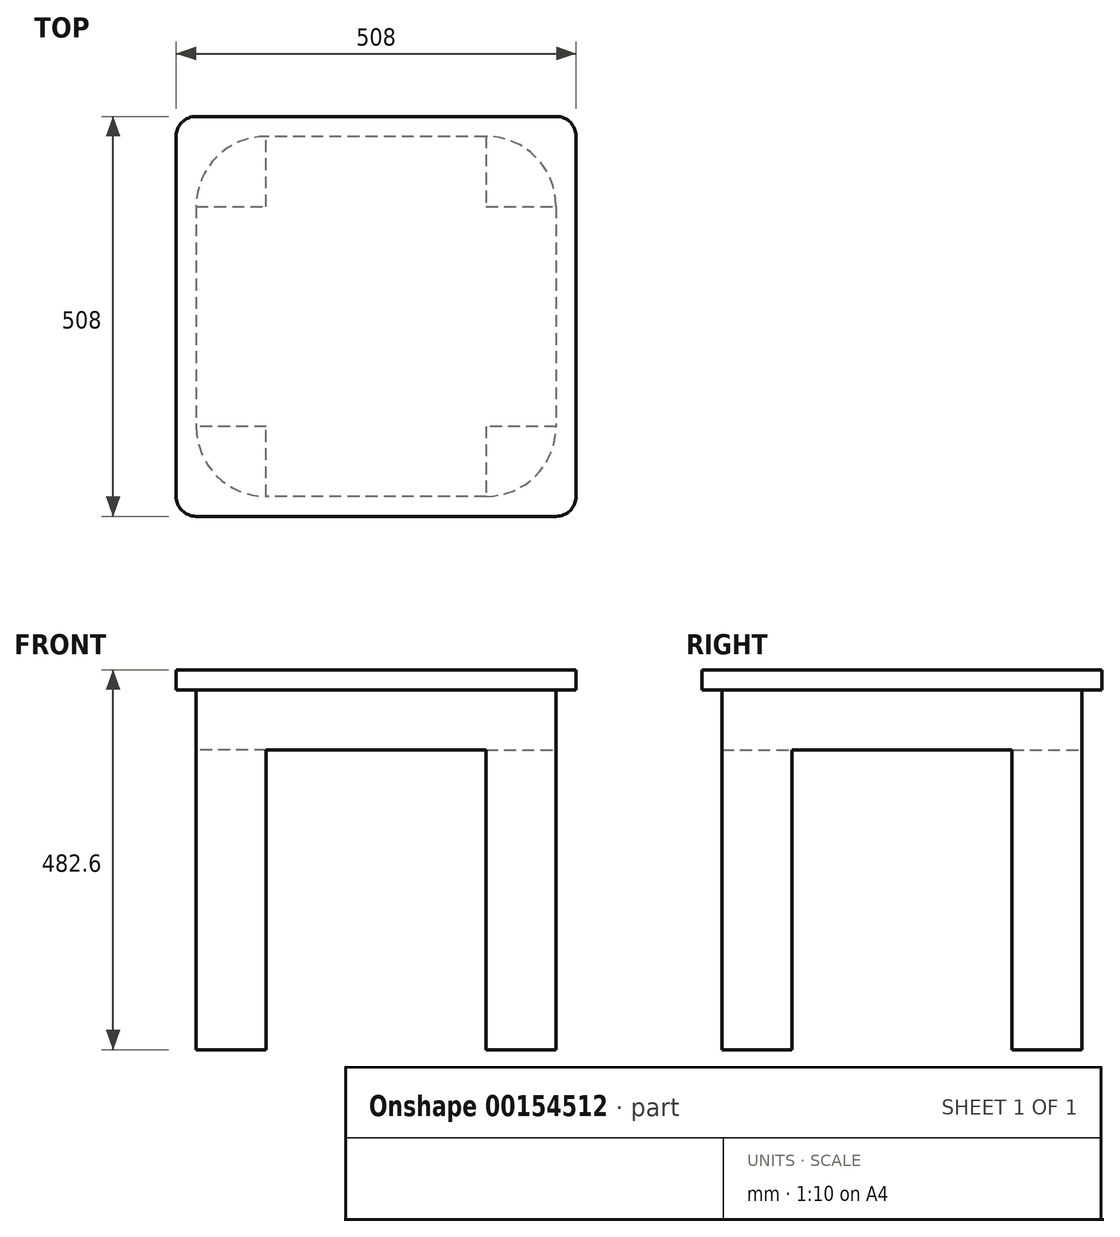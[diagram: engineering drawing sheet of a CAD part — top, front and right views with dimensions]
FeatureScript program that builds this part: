
annotation { "Feature Type Name" : "Feature", "Feature Type Description" : "" }
export const myFeature = defineFeature(function(context is Context, id is Id, definition is map)
    precondition{}
    {
        {
            var Q0;
            Q0=qCreatedBy(makeId("Top.planeOp"),FACE);
            var sketch = newSketch(context, id + "F0", { "sketchPlane" : qUnion([Q0])});
            skLineSegment(sketch, "E0.bottom", {"start": v(254, 254) * mm, "end": v(-254, 254) * mm});
            skLineSegment(sketch, "E0.top", {"start": v(254, -254) * mm, "end": v(-254, -254) * mm});
            skLineSegment(sketch, "E0.left", {"start": v(254, 254) * mm, "end": v(254, -254) * mm});
            skLineSegment(sketch, "E0.right", {"start": v(-254, 254) * mm, "end": v(-254, -254) * mm});
            skPoint(sketch, "E0.middle", {"position": v(0, 0) * mm});
            skLineSegment(sketch, "E1.bottom", {"start": v(228.6, 228.6) * mm, "end": v(-228.6, 228.6) * mm});
            skLineSegment(sketch, "E1.top", {"start": v(228.6, -228.6) * mm, "end": v(-228.6, -228.6) * mm});
            skLineSegment(sketch, "E1.left", {"start": v(228.6, 228.6) * mm, "end": v(228.6, -228.6) * mm});
            skLineSegment(sketch, "E1.right", {"start": v(-228.6, 228.6) * mm, "end": v(-228.6, -228.6) * mm});
            skLineSegment(sketch, "E2", {"start": v(-228.6, 139.7) * mm, "end": v(-139.7, 139.7) * mm});
            skLineSegment(sketch, "E3", {"start": v(-139.7, 139.7) * mm, "end": v(-139.7, 228.6) * mm});
            skLineSegment(sketch, "E4", {"start": v(139.7, 228.6) * mm, "end": v(139.7, 139.7) * mm});
            skLineSegment(sketch, "E5", {"start": v(139.7, 139.7) * mm, "end": v(228.6, 139.7) * mm});
            skLineSegment(sketch, "E6", {"start": v(228.6, -139.7) * mm, "end": v(139.7, -139.7) * mm});
            skLineSegment(sketch, "E7", {"start": v(139.7, -139.7) * mm, "end": v(139.7, -228.6) * mm});
            skLineSegment(sketch, "E8", {"start": v(-139.7, -228.6) * mm, "end": v(-139.7, -139.7) * mm});
            skLineSegment(sketch, "E9", {"start": v(-139.7, -139.7) * mm, "end": v(-228.6, -139.7) * mm});
            skSolve(sketch);
        }
        {
            var Q0;
            Q0=makeQuery(id+"F0.imprint","IMPRINT",FACE,{"disambiguationData":[TD([[makeQuery(id+"F0.imprint","IMPRINT",EDGE,{"derivedFrom":sQuery(id+"F0.wireOp",EDGE,"E0.bottom")}),1.0]])]});
            var Q1;
            {var subQ3=sQuery(id+"F0.wireOp",EDGE,"E8");Q1=makeQuery(id+"F0.imprint","IMPRINT",FACE,{"disambiguationData":[TD([[makeQuery(id+"F0.imprint","IMPRINT",EDGE,{"derivedFrom":subQ3}),1.0]])]});}
            var Q2;
            {var subQ4=sQuery(id+"F0.wireOp",EDGE,"E6");Q2=makeQuery(id+"F0.imprint","IMPRINT",FACE,{"disambiguationData":[TD([[makeQuery(id+"F0.imprint","IMPRINT",EDGE,{"derivedFrom":subQ4}),1.0]])]});}
            var Q3;
            {var subQ3=sQuery(id+"F0.wireOp",EDGE,"E4");Q3=makeQuery(id+"F0.imprint","IMPRINT",FACE,{"disambiguationData":[TD([[makeQuery(id+"F0.imprint","IMPRINT",EDGE,{"derivedFrom":subQ3}),1.0]])]});}
            var Q4;
            {var subQ4=sQuery(id+"F0.wireOp",EDGE,"E2");Q4=makeQuery(id+"F0.imprint","IMPRINT",FACE,{"disambiguationData":[TD([[makeQuery(id+"F0.imprint","IMPRINT",EDGE,{"derivedFrom":subQ4}),1.0]])]});}
            var Q5;
            {var subQ3=sQuery(id+"F0.wireOp",EDGE,"E2");Q5=makeQuery(id+"F0.imprint","IMPRINT",FACE,{"disambiguationData":[TD([[makeQuery(id+"F0.imprint","IMPRINT",EDGE,{"derivedFrom":subQ3}),-1.0]])]});}
            extrude(context, id + "F1", {"entities" : qUnion([Q0, Q1, Q2, Q3, Q4, Q5]), "oppositeDirection" : true, "depth" : 25.4 * mm});
        }
        {
            var Q0;
            {var subQ4=sQuery(id+"F0.wireOp",EDGE,"E2");Q0=makeQuery(id+"F0.imprint","IMPRINT",FACE,{"disambiguationData":[TD([[makeQuery(id+"F0.imprint","IMPRINT",EDGE,{"derivedFrom":subQ4}),1.0]])]});}
            var Q1;
            {var subQ3=sQuery(id+"F0.wireOp",EDGE,"E2");Q1=makeQuery(id+"F0.imprint","IMPRINT",FACE,{"disambiguationData":[TD([[makeQuery(id+"F0.imprint","IMPRINT",EDGE,{"derivedFrom":subQ3}),-1.0]])]});}
            var Q2;
            {var subQ3=sQuery(id+"F0.wireOp",EDGE,"E4");Q2=makeQuery(id+"F0.imprint","IMPRINT",FACE,{"disambiguationData":[TD([[makeQuery(id+"F0.imprint","IMPRINT",EDGE,{"derivedFrom":subQ3}),1.0]])]});}
            var Q3;
            {var subQ4=sQuery(id+"F0.wireOp",EDGE,"E6");Q3=makeQuery(id+"F0.imprint","IMPRINT",FACE,{"disambiguationData":[TD([[makeQuery(id+"F0.imprint","IMPRINT",EDGE,{"derivedFrom":subQ4}),1.0]])]});}
            var Q4;
            {var subQ3=sQuery(id+"F0.wireOp",EDGE,"E8");Q4=makeQuery(id+"F0.imprint","IMPRINT",FACE,{"disambiguationData":[TD([[makeQuery(id+"F0.imprint","IMPRINT",EDGE,{"derivedFrom":subQ3}),1.0]])]});}
            extrude(context, id + "F2", {"entities" : qUnion([Q0, Q1, Q2, Q3, Q4]), "operationType" : NewBodyOperationType.ADD, "oppositeDirection" : true, "depth" : 101.6 * mm});
        }
        {
            var Q0;
            {var subQ4=sQuery(id+"F0.wireOp",EDGE,"E2");Q0=makeQuery(id+"F0.imprint","IMPRINT",FACE,{"disambiguationData":[TD([[makeQuery(id+"F0.imprint","IMPRINT",EDGE,{"derivedFrom":subQ4}),1.0]])]});}
            var Q1;
            {var subQ3=sQuery(id+"F0.wireOp",EDGE,"E8");Q1=makeQuery(id+"F0.imprint","IMPRINT",FACE,{"disambiguationData":[TD([[makeQuery(id+"F0.imprint","IMPRINT",EDGE,{"derivedFrom":subQ3}),1.0]])]});}
            var Q2;
            {var subQ3=sQuery(id+"F0.wireOp",EDGE,"E4");Q2=makeQuery(id+"F0.imprint","IMPRINT",FACE,{"disambiguationData":[TD([[makeQuery(id+"F0.imprint","IMPRINT",EDGE,{"derivedFrom":subQ3}),1.0]])]});}
            var Q3;
            {var subQ4=sQuery(id+"F0.wireOp",EDGE,"E6");Q3=makeQuery(id+"F0.imprint","IMPRINT",FACE,{"disambiguationData":[TD([[makeQuery(id+"F0.imprint","IMPRINT",EDGE,{"derivedFrom":subQ4}),1.0]])]});}
            extrude(context, id + "F3", {"entities" : qUnion([Q0, Q1, Q2, Q3]), "operationType" : NewBodyOperationType.ADD, "oppositeDirection" : true, "depth" : 482.6 * mm});
        }
        {
            var Q0;
            {var subQ0=sQuery(id+"F0.wireOp",EDGE,"E1.right");var subQ1=sQuery(id+"F0.wireOp",EDGE,"E1.top");Q0=makeQuery(id+"F3.boolean.opBoolean","MERGE",EDGE,{"derivedFrom":[makeQuery(id+"F2.opExtrude","SWEPT_EDGE",EDGE,{"disambiguationData":[OSD([subQ1,subQ0])]}),makeQuery(id+"F3.opExtrude","SWEPT_EDGE",EDGE,{"disambiguationData":[OSD([subQ1,subQ0])]})]});}
            var Q1;
            {var subQ0=sQuery(id+"F0.wireOp",EDGE,"E1.left");var subQ1=sQuery(id+"F0.wireOp",EDGE,"E1.top");Q1=makeQuery(id+"F3.boolean.opBoolean","MERGE",EDGE,{"derivedFrom":[makeQuery(id+"F2.opExtrude","SWEPT_EDGE",EDGE,{"disambiguationData":[OSD([subQ1,subQ0])]}),makeQuery(id+"F3.opExtrude","SWEPT_EDGE",EDGE,{"disambiguationData":[OSD([subQ1,subQ0])]})]});}
            var Q2;
            {var subQ0=sQuery(id+"F0.wireOp",EDGE,"E1.left");var subQ1=sQuery(id+"F0.wireOp",EDGE,"E1.bottom");Q2=makeQuery(id+"F3.boolean.opBoolean","MERGE",EDGE,{"derivedFrom":[makeQuery(id+"F2.opExtrude","SWEPT_EDGE",EDGE,{"disambiguationData":[OSD([subQ1,subQ0])]}),makeQuery(id+"F3.opExtrude","SWEPT_EDGE",EDGE,{"disambiguationData":[OSD([subQ1,subQ0])]})]});}
            var Q3;
            {var subQ0=sQuery(id+"F0.wireOp",EDGE,"E1.right");var subQ1=sQuery(id+"F0.wireOp",EDGE,"E1.bottom");Q3=makeQuery(id+"F3.boolean.opBoolean","MERGE",EDGE,{"derivedFrom":[makeQuery(id+"F2.opExtrude","SWEPT_EDGE",EDGE,{"disambiguationData":[OSD([subQ1,subQ0])]}),makeQuery(id+"F3.opExtrude","SWEPT_EDGE",EDGE,{"disambiguationData":[OSD([subQ1,subQ0])]})]});}
            fillet(context, id + "F4", {"entities" : qUnion([Q0, Q1, Q2, Q3]), "radius" : 88.9 * mm, "tangentPropagation" : true, "allowEdgeOverflow" : false});
        }
        {
            var Q0;
            Q0=makeQuery(id+"F1.opExtrude","SWEPT_EDGE",EDGE,{"disambiguationData":[OSD([sQuery(id+"F0.wireOp",EDGE,"E0.top"),sQuery(id+"F0.wireOp",EDGE,"E0.left")])]});
            var Q1;
            Q1=makeQuery(id+"F1.opExtrude","SWEPT_EDGE",EDGE,{"disambiguationData":[OSD([sQuery(id+"F0.wireOp",EDGE,"E0.bottom"),sQuery(id+"F0.wireOp",EDGE,"E0.left")])]});
            var Q2;
            Q2=makeQuery(id+"F1.opExtrude","SWEPT_EDGE",EDGE,{"disambiguationData":[OSD([sQuery(id+"F0.wireOp",EDGE,"E0.bottom"),sQuery(id+"F0.wireOp",EDGE,"E0.right")])]});
            var Q3;
            Q3=makeQuery(id+"F1.opExtrude","SWEPT_EDGE",EDGE,{"disambiguationData":[OSD([sQuery(id+"F0.wireOp",EDGE,"E0.top"),sQuery(id+"F0.wireOp",EDGE,"E0.right")])]});
            fillet(context, id + "F5", {"entities" : qUnion([Q0, Q1, Q2, Q3]), "radius" : 25.4 * mm, "tangentPropagation" : true, "allowEdgeOverflow" : false});
        }
    });
